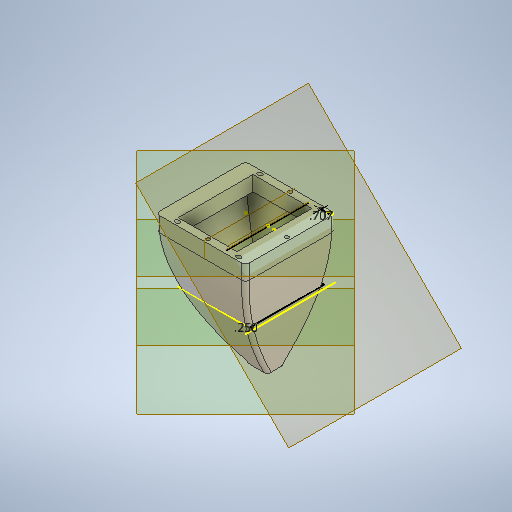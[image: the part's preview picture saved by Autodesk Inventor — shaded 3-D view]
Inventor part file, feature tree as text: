
AUTODESK INVENTOR PART (.ipt)
format: ipt  version: 2025.1 (Build 291241020, 241B)  size: 732,160 bytes
history: native  units: in
note: dims shown in document units (in); Inventor stores cm internally (conversion verified against a paired STEP export)
features: sketch x21, extrude x10, plane x6, fillet x4, loft x1, shell x1, mirror x1, other x1
ambient origin geometry x8: Origin, YZ Plane, XZ Plane, XY Plane, X Axis, Y Axis, Z Axis, Center Point
bodies: Solid1 (feature_tree)
feature tree (45):
  sketch  "Sketch1"  dims[d0=6.0in d1=6.0in]
  plane  "Work Plane1"
  plane  "Work Plane2"
  sketch  "Sketch2"  dims[d2=5.5in d7=8.0in d10=1.0in d11=0.0in d12=4.0in]
  extrude  "Extrusion1"  Depth=6.0in
  sketch  "3D Sketch1"
  plane  "Work Plane3"
  sketch  "Sketch3"  dims[d24=0.6in d25=0.6in]
  loft  "Loft1"
  sketch  "Sketch4"  dims[d26=0.0in d27=90.0deg d28=0.0in d29=90.0deg d30=0.0in d31=90.0deg d32=0.0in d33=90.0deg d38=0.25in d39=0.0in d40=90.0deg]
  fillet  "Fillet1"  Radius=1.0in
  fillet  "Fillet2"  Radius=4.0in
  extrude  "Extrusion3"  Depth=0.6in
  extrude  "Extrusion4"  Depth=0.25in
  shell  "Shell2"  Thickness=0.0in
  extrude  "Extrusion5"  Depth=0.25in
  sketch  "Sketch9"  dims[d64=0.712in d65=0.712in]
  fillet  "Fillet3"  Radius=0.25in
  fillet  "Fillet4"  Radius=0.5in
  extrude  "Extrusion7"  Depth=0.25in
  plane  "Work Plane4"
  sketch  "Sketch10"  dims[d66=0.726in d67=0.1in d68=0.0in]
  sketch  "Sketch11"  dims[d72=0.3in d73=0.25in]
  sketch  "Sketch12"  dims[d76=0.175in d77=0.175in]
  extrude  "Extrusion8"  Depth=2.5in
  sketch  "Sketch14"  dims[d80=1.0in]
  plane  "Work Plane5"
  extrude  "Extrusion9"  Depth=0.712in
  plane  "Work Plane6"
  mirror  "Mirror1"
  extrude  "Extrusion10"  Depth=0.1in TaperAngle=0.0deg
  sketch  "Sketch17"  dims[d84=45.0deg]
  sketch  "Sketch18"  dims[d85=0.25in]
  extrude  "Extrusion11"  Depth=0.25in
  extrude  "Extrusion12"  Depth=0.175in
  sketch  "3D Sketch7"
  other  "Edges1"
  sketch  "Sketch5"  dims[d41=0.0in d42=90.0deg d44=0.25in d45=0.25in d51=0.5in d52=0.0in]
  sketch  "Sketch7"  dims[d58=0.5in d59=0.0in d60=0.25in]
  sketch  "Sketch8"  dims[d61=2.5in d62=2.5in]
  sketch  "Sketch13"  dims[d78=12.0in d79=0.0in]
  sketch  "Sketch15"  dims[d81=1.0in d82=0.0in]
  sketch  "Sketch16"  dims[d83=0.707in]
  sketch  "Sketch19"  dims[d86=1.0in d87=0.75in d88=0.0in d89=0.0in]
  sketch  "Sketch20"  dims[d90=-2.75in d91=0.175in d92=1.0in d93=1.0in d94=0.205in d95=0.205in d96=0.205in d97=0.205in d98=0.157in d99=0.0in d102=0.7in d103=0.3in d106=0.502in d107=0.502in d108=1.004in d109=0.205in d110=0.205in d111=0.205in d112=0.205in d113=0.157in d114=0.0in d115=2.5in d116=1.0in d117=0.0in d53=0.5in d54=0.0344in d74=0.0in d75=0.0in]
